# Revit family: Ulimax_Madeira_Porta-de-Giro-1-Folha
name_source: partatom
category: Portas
units: mm (PartAtom-declared; Revit-internal decimal feet)

## family parameters
Compartilhado = Não
Corte com vazios quando carregada = Não
Hospedeiro = Parede
Número OmniClass = 23.30.10.00
Ponto de cálculo do ambiente = Não
Sempre na vertical = Sim
Título OmniClass = Doors

## types (12) — shared parameters
4.5cm = Sim
5.5cm = Não
6.5cm = Não
Altura = 210
Altura Maçaneta = 110
Altura bruta = 220
Comentários de tipos = Porta de Giro de Madeira
Construção analítica = <Nenhum>
Definir propriedades térmicas por = Tipo esquemático
Descrição = Porta com esquadria de madeira, 1 Folha
Developer = Blocks
Espessura = 4.5
Espessura     ‎ = 1.3
Fabricante = Ulimax - Wood & Aluminum
Fechamento da parede = Por hospedeiro
Largura‎ ‎ = 7
Maçaneta ‎ ‎ = Ulimax - Metal - Chrome - 203-203-203
URL = https://www.ulimax.com.br
URL Developer = https://BlocksRvt.com
URL Produto = https://www.ulimax.com.br
URL Template = https://www.ulimax.com.br

## per-type parameters (varying)
| type | Batente | Folha | Guarnição | Largura | Largura bruta |
| Cedro Arana - 0.70 x 2.10 | Ulimax - Wood - Freijo | Ulimax - Wood - Freijo | Ulimax - Wood - Freijo | 90 | 100 |
| Cedro Arana - 0.80 x 2.10 | Ulimax - Wood - Cedro Arana | Ulimax - Wood - Cedro Arana | Ulimax - Wood - Cedro Arana | 80 | 90 |
| Cedro Arana - 0.90 x 2.10 | Ulimax - Wood - Cedro Arana | Ulimax - Wood - Cedro Arana | Ulimax - Wood - Cedro Arana | 90 | 100 |
| Cedro Arana - 0.60 x 2.10 | Ulimax - Wood - Cedro Arana | Ulimax - Wood - Cedro Arana | Ulimax - Wood - Cedro Arana | 60 | 70 |
| Cumarú - 0.70 x 2.10 | Ulimax - Wood - Cumarú | Ulimax - Wood - Cumarú | Ulimax - Wood - Cumarú | 70 | 80 |
| Cumarú - 0.60 x 2.10 | Ulimax - Wood - Cumarú | Ulimax - Wood - Cumarú | Ulimax - Wood - Cumarú | 60 | 70 |
| Cumarú - 0.80 x 2.10 | Ulimax - Wood - Cumarú | Ulimax - Wood - Cumarú | Ulimax - Wood - Cumarú | 80 | 90 |
| Cumarú - 0.90 x 2.10 | Ulimax - Wood - Cumarú | Ulimax - Wood - Cumarú | Ulimax - Wood - Cumarú | 90 | 100 |
| Freijó - 0.70 x 2.10 | Ulimax - Wood - Freijo | Ulimax - Wood - Freijo | Ulimax - Wood - Freijo | 70 | 80 |
| Freijó - 0.80 x 2.10 | Ulimax - Wood - Freijo | Ulimax - Wood - Freijo | Ulimax - Wood - Freijo | 80 | 90 |
| Freijó - 0.90 x 2.10 | Ulimax - Wood - Freijo | Ulimax - Wood - Freijo | Ulimax - Wood - Freijo | 90 | 100 |
| Freijó - 0.60 x 2.10 | Ulimax - Wood - Freijo | Ulimax - Wood - Freijo | Ulimax - Wood - Freijo | 60 | 70 |
